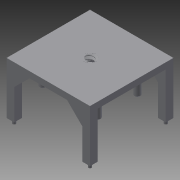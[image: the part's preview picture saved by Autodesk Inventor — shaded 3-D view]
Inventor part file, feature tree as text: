
AUTODESK INVENTOR PART (.ipt)
format: ipt  version: 2015 (Build 190159000, 159)  size: 397,824 bytes
history: native  units: in
note: dims shown in document units (in); Inventor stores cm internally (conversion verified against a paired STEP export)
features: sketch x7, projected_geometry x6, extrude x5, reference x3, chamfer x2, thread x1, revolve x1, helix x1
ambient origin geometry x8: Origin, YZ Plane, XZ Plane, XY Plane, X Axis, Y Axis, Z Axis, Center Point
bodies: Solid1 (feature_tree), Solid3 (feature_tree)
feature tree (26):
  extrude  "Extrusion1"  Depth=0.1969in
  extrude  "Extrusion2"  Depth=0.0001in
  chamfer  "Chamfer1"  Distance=0.1575in
  extrude  "Extrusion3"  Depth=0.3937in
  extrude  "Extrusion4"  Depth=0.1535in
  chamfer  "Chamfer2"  Distance=0.5906in
  thread  "Thread1"  [1 undecoded]
  extrude  "Extrusion5"  TaperAngle=60.0deg  [1 undecoded]
  revolve  "Revolution2"  [1 undecoded]
  helix  "Coil2"  [1 undecoded]
  sketch  "Sketch1"  dims[d0=0.1969in d1=0.1969in]
  reference  "Reference1"
  reference  "Reference2"
  reference  "Reference3"
  sketch  "Sketch2"  dims[d2=1.1811in d3=0.0in d4=0.0001in d7=0.1575in d8=0.0in]
  sketch  "Sketch3"  dims[d9=0.3937in d10=0.0787in d11=45.0deg d12=0.3189in]
  projected_geometry  "Projected Loop1"
  sketch  "Sketch4"  dims[d13=0.1969in d14=0.0in d15=0.1535in]
  projected_geometry  "Projected Loop2"
  sketch  "Sketch7"  dims[d16=1.0236in]
  projected_geometry  "Projected Loop3"
  projected_geometry  "Projected Loop4"
  projected_geometry  "Projected Loop5"
  projected_geometry  "Projected Loop6"
  sketch  "Sketch8"  dims[d17=1.4173in d18=0.5906in d19=0.0in d20=0.0394in d21=0.0787in d22=45.0deg]
  sketch  "Sketch9"  dims[d23=0.3937in d24=0.0in d32=60.0deg d43=0.0787in d46=1.95in d47=1.95in d48=0.1181in d49=0.0in d50=60.0deg d51=0.0133in d52=0.0133in d55=0.0833in d57=60.0deg d59=0.0in d60=0.0834in d61=0.3241in d62=0.3937in d63=0.0in d64=0.0in d65=0.0in d66=0.0in d67=0.0in]
note: 4 required parameter values undecoded (feature->parameter linkage not recoverable at this tier; creation-order binding heuristic only, values carry confidence <= 0.55)